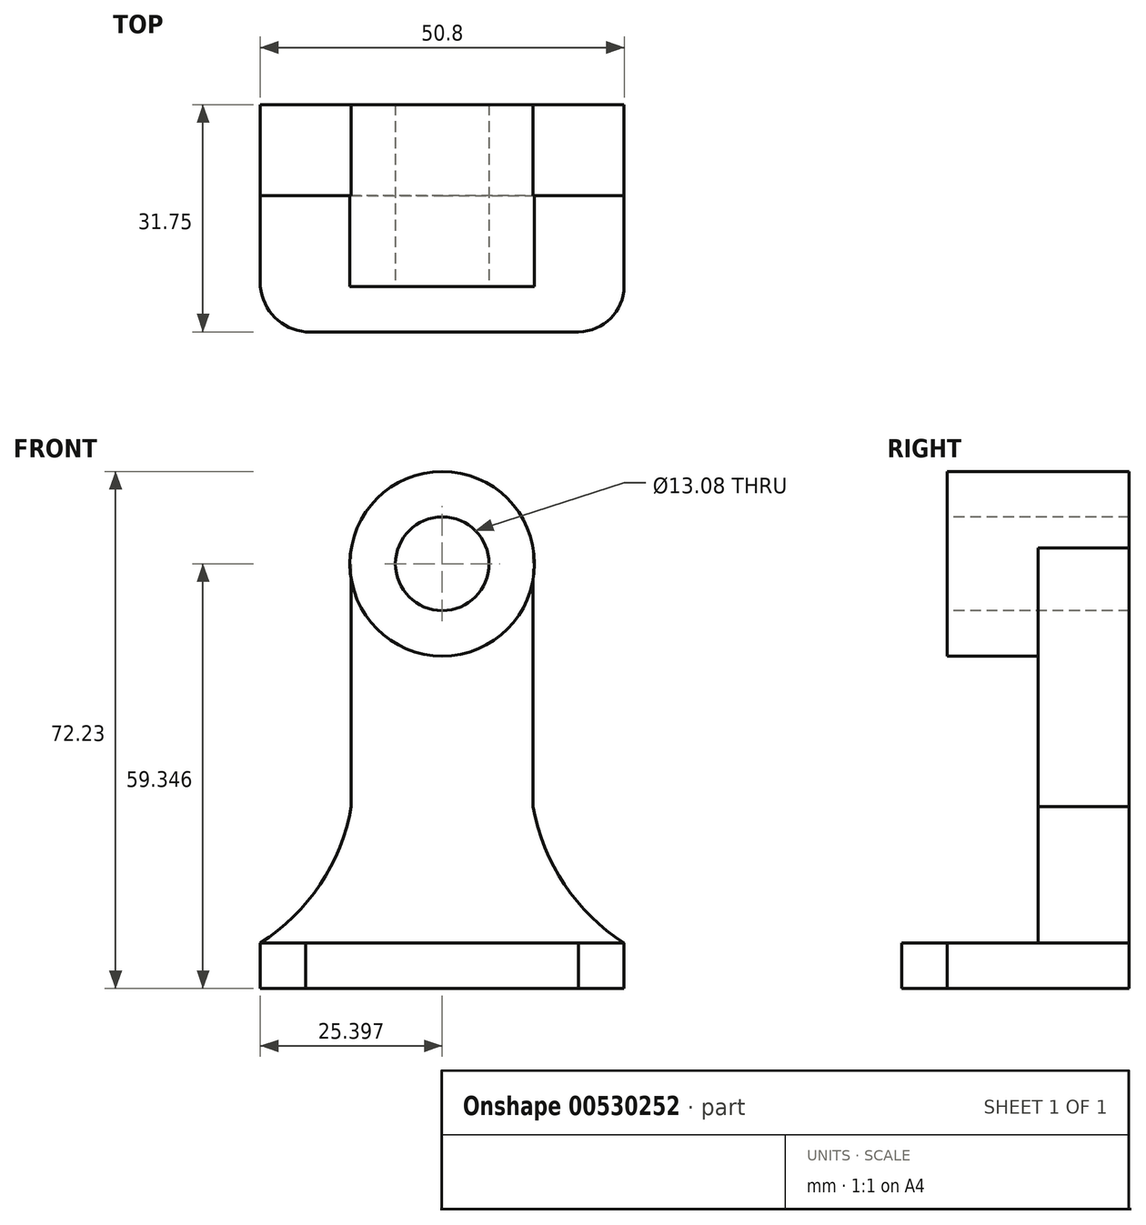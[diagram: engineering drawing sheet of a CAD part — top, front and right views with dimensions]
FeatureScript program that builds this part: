
annotation { "Feature Type Name" : "Feature", "Feature Type Description" : "" }
export const myFeature = defineFeature(function(context is Context, id is Id, definition is map)
    precondition{}
    {
        {
            var Q0;
            Q0=qCreatedBy(makeId("Front.planeOp"),FACE);
            var sketch = newSketch(context, id + "F0", { "sketchPlane" : qUnion([Q0])});
            skLineSegment(sketch, "E0", {"start": v(-66.08, 0) * mm, "end": v(-15.28, 0) * mm});
            skLineSegment(sketch, "E1", {"start": v(-15.28, 0) * mm, "end": v(-15.28, 6.35) * mm});
            skLineSegment(sketch, "E2", {"start": v(-15.28, 6.35) * mm, "end": v(-66.08, 6.35) * mm});
            skLineSegment(sketch, "E3", {"start": v(-66.08, 6.35) * mm, "end": v(-66.08, 0) * mm});
            skSolve(sketch);
        }
        {
            var Q0;
            Q0 = qSketchRegion(id + "F0", true);
            extrude(context, id + "F1", {"entities" : qUnion([Q0]), "depth" : 31.75 * mm, "offsetDistance" : 25.4 * mm});
        }
        {
            var Q0;
            Q0=makeQuery(id+"F1.opExtrude","CAP_FACE",FACE,{"disambiguationData":[OSD([sQuery(id+"F0.wireOp",EDGE,"E0"),sQuery(id+"F0.wireOp",EDGE,"E1"),sQuery(id+"F0.wireOp",EDGE,"E2"),sQuery(id+"F0.wireOp",EDGE,"E3")])],"isStart":true});
            var sketch = newSketch(context, id + "F2", { "sketchPlane" : qUnion([Q0])});
            skLineSegment(sketch, "E4", {"start": v(15.28, 6.35) * mm, "end": v(15.28, 76.2) * mm});
            skLineSegment(sketch, "E5", {"start": v(15.28, 76.2) * mm, "end": v(66.08, 76.2) * mm});
            skLineSegment(sketch, "E6", {"start": v(66.08, 76.2) * mm, "end": v(66.08, 6.35) * mm});
            skLineSegment(sketch, "E7", {"start": v(66.08, 6.35) * mm, "end": v(15.28, 6.35) * mm});
            skSolve(sketch);
        }
        {
            var Q0;
            Q0 = qSketchRegion(id + "F2", true);
            extrude(context, id + "F3", {"entities" : qUnion([Q0]), "operationType" : NewBodyOperationType.ADD, "oppositeDirection" : true, "depth" : 12.7 * mm, "offsetDistance" : 25.4 * mm});
        }
        {
            var Q0;
            Q0=makeQuery(id+"F3.opExtrude","CAP_FACE",FACE,{"disambiguationData":[OSD([sQuery(id+"F2.wireOp",EDGE,"E4"),sQuery(id+"F2.wireOp",EDGE,"E5"),sQuery(id+"F2.wireOp",EDGE,"E6"),sQuery(id+"F2.wireOp",EDGE,"E7")])],"isStart":false});
            var sketch = newSketch(context, id + "F4", { "sketchPlane" : qUnion([Q0])});
            skLineSegment(sketch, "E8", {"start": v(-53.38, 76.2) * mm, "end": v(-53.38, 6.35) * mm});
            skLineSegment(sketch, "E9", {"start": v(-53.38, 6.35) * mm, "end": v(-27.98, 6.35) * mm});
            skLineSegment(sketch, "E10", {"start": v(-27.98, 6.35) * mm, "end": v(-27.98, 76.2) * mm});
            skLineSegment(sketch, "E11", {"start": v(-27.98, 76.2) * mm, "end": v(-53.38, 76.2) * mm});
            skSolve(sketch);
        }
        {
            var Q0;
            {var subQ0=sQuery(id+"F4.wireOp",EDGE,"E8");Q0=makeQuery(id+"F4.imprint","IMPRINT",FACE,{"disambiguationData":[TD([[makeQuery(id+"F4.imprint","IMPRINT",EDGE,{"derivedFrom":subQ0}),-1.0]])]});}
            var Q1;
            {var subQ0=sQuery(id+"F4.wireOp",EDGE,"E10");Q1=makeQuery(id+"F4.imprint","IMPRINT",FACE,{"disambiguationData":[TD([[makeQuery(id+"F4.imprint","IMPRINT",EDGE,{"derivedFrom":subQ0}),-1.0]])]});}
            extrude(context, id + "F5", {"entities" : qUnion([Q0, Q1]), "operationType" : NewBodyOperationType.REMOVE, "oppositeDirection" : true, "depth" : 25.4 * mm, "offsetDistance" : 25.4 * mm});
        }
        {
            var Q0;
            Q0=makeQuery(id+"F3.boolean.opBoolean","MERGE",FACE,{"derivedFrom":[makeQuery(id+"F1.opExtrude","CAP_FACE",FACE,{"disambiguationData":[OSD([sQuery(id+"F0.wireOp",EDGE,"E0"),sQuery(id+"F0.wireOp",EDGE,"E1"),sQuery(id+"F0.wireOp",EDGE,"E2"),sQuery(id+"F0.wireOp",EDGE,"E3")])],"isStart":true}),makeQuery(id+"F3.opExtrude","CAP_FACE",FACE,{"disambiguationData":[OSD([sQuery(id+"F2.wireOp",EDGE,"E4"),sQuery(id+"F2.wireOp",EDGE,"E5"),sQuery(id+"F2.wireOp",EDGE,"E6"),sQuery(id+"F2.wireOp",EDGE,"E7")])],"isStart":true})]});
            var sketch = newSketch(context, id + "F6", { "sketchPlane" : qUnion([Q0])});
            skArc(sketch, "E12", {"start": v(15.28, 6.35) * mm, "mid": v(23.62, 14.55) * mm, "end": v(27.98, 25.4) * mm});
            skArc(sketch, "E13", {"start": v(53.38, 25.4) * mm, "mid": v(57.74, 14.55) * mm, "end": v(66.08, 6.35) * mm});
            skSolve(sketch);
        }
        {
            var Q0;
            Q0 = qSketchRegion(id + "F6", true);
            var Q1;
            {var subQ0=sQuery(id+"F6.wireOp",EDGE,"E12");Q1=makeQuery(id+"F6.imprint","IMPRINT",FACE,{"disambiguationData":[TD([[makeQuery(id+"F6.imprint","IMPRINT",EDGE,{"derivedFrom":subQ0}),-1.0]])]});}
            var Q2;
            {var subQ0=sQuery(id+"F6.wireOp",EDGE,"E13");Q2=makeQuery(id+"F6.imprint","IMPRINT",FACE,{"disambiguationData":[TD([[makeQuery(id+"F6.imprint","IMPRINT",EDGE,{"derivedFrom":subQ0}),-1.0]])]});}
            extrude(context, id + "F7", {"entities" : qUnion([Q0, Q1, Q2]), "operationType" : NewBodyOperationType.ADD, "oppositeDirection" : true, "depth" : 12.7 * mm, "offsetDistance" : 25.4 * mm});
        }
        {
            var Q0;
            {var subQ0=sQuery(id+"F2.wireOp",EDGE,"E7");var subQ1=sQuery(id+"F2.wireOp",EDGE,"E6");var subQ2=sQuery(id+"F2.wireOp",EDGE,"E5");var subQ3=sQuery(id+"F2.wireOp",EDGE,"E4");var subQ4=sQuery(id+"F0.wireOp",EDGE,"E3");var subQ5=sQuery(id+"F0.wireOp",EDGE,"E2");var subQ6=sQuery(id+"F0.wireOp",EDGE,"E1");var subQ7=sQuery(id+"F0.wireOp",EDGE,"E0");Q0=makeQuery(id+"F7.boolean.opBoolean","MERGE",FACE,{"derivedFrom":[makeQuery(id+"F3.opExtrude","CAP_FACE",FACE,{"disambiguationData":[OSD([subQ3,subQ2,subQ1,subQ0])],"isStart":false}),makeQuery(id+"F7.opExtrude","CAP_FACE",FACE,{"disambiguationData":[OSD([subQ7,subQ6,subQ5,subQ4,subQ3,subQ2,subQ1,subQ0,sQuery(id+"F4.wireOp",EDGE,"E10"),sQuery(id+"F6.wireOp",EDGE,"E12")])],"isStart":false}),makeQuery(id+"F7.opExtrude","CAP_FACE",FACE,{"disambiguationData":[OSD([subQ7,subQ6,subQ5,subQ4,subQ3,subQ2,subQ1,subQ0,sQuery(id+"F4.wireOp",EDGE,"E8"),sQuery(id+"F6.wireOp",EDGE,"E13")])],"isStart":false})]});}
            var sketch = newSketch(context, id + "F8", { "sketchPlane" : qUnion([Q0])});
            skArc(sketch, "E14", {"start": v(-27.98, 57.15) * mm, "mid": v(-40.68, 72.23) * mm, "end": v(-53.38, 57.15) * mm});
            skSolve(sketch);
        }
        {
            var Q0;
            {var subQ5=makeQuery(id+"F3.opExtrude","CAP_EDGE",EDGE,{"disambiguationData":[OSD([sQuery(id+"F2.wireOp",EDGE,"E5")])],"isStart":false});Q0=makeQuery(id+"F8.imprint","IMPRINT",FACE,{"disambiguationData":[TD([[makeQuery(id+"F8.imprint","IMPRINT",EDGE,{"derivedFrom":subQ5}),1.0]])]});}
            extrude(context, id + "F9", {"entities" : qUnion([Q0]), "operationType" : NewBodyOperationType.REMOVE, "endBound" : BoundingType.THROUGH_ALL, "oppositeDirection" : true, "depth" : 25.4 * mm, "offsetDistance" : 25.4 * mm});
        }
        {
            var Q0;
            {var subQ0=sQuery(id+"F2.wireOp",EDGE,"E7");var subQ1=sQuery(id+"F2.wireOp",EDGE,"E6");var subQ2=sQuery(id+"F2.wireOp",EDGE,"E5");var subQ3=sQuery(id+"F2.wireOp",EDGE,"E4");var subQ4=sQuery(id+"F0.wireOp",EDGE,"E3");var subQ5=sQuery(id+"F0.wireOp",EDGE,"E2");var subQ6=sQuery(id+"F0.wireOp",EDGE,"E1");var subQ7=sQuery(id+"F0.wireOp",EDGE,"E0");Q0=makeQuery(id+"F7.boolean.opBoolean","MERGE",FACE,{"derivedFrom":[makeQuery(id+"F3.opExtrude","CAP_FACE",FACE,{"disambiguationData":[OSD([subQ3,subQ2,subQ1,subQ0])],"isStart":false}),makeQuery(id+"F7.opExtrude","CAP_FACE",FACE,{"disambiguationData":[OSD([subQ7,subQ6,subQ5,subQ4,subQ3,subQ2,subQ1,subQ0,sQuery(id+"F4.wireOp",EDGE,"E10"),sQuery(id+"F6.wireOp",EDGE,"E12")])],"isStart":false}),makeQuery(id+"F7.opExtrude","CAP_FACE",FACE,{"disambiguationData":[OSD([subQ7,subQ6,subQ5,subQ4,subQ3,subQ2,subQ1,subQ0,sQuery(id+"F4.wireOp",EDGE,"E8"),sQuery(id+"F6.wireOp",EDGE,"E13")])],"isStart":false})]});}
            var sketch = newSketch(context, id + "F10", { "sketchPlane" : qUnion([Q0])});
            skCircle(sketch, "E15", {"center": v(-40.68, 59.35) * mm, "radius": 12.89 * mm});
            skSolve(sketch);
        }
        {
            var Q0;
            Q0 = qSketchRegion(id + "F10", true);
            extrude(context, id + "F11", {"entities" : qUnion([Q0]), "operationType" : NewBodyOperationType.ADD, "depth" : 12.7 * mm, "offsetDistance" : 25.4 * mm});
        }
        {
            var Q0;
            Q0=makeQuery(id+"F11.opExtrude","CAP_FACE",FACE,{"disambiguationData":[OSD([sQuery(id+"F10.wireOp",EDGE,"E15")])],"isStart":false});
            var sketch = newSketch(context, id + "F12", { "sketchPlane" : qUnion([Q0])});
            skCircle(sketch, "E16", {"center": v(-40.68, 59.35) * mm, "radius": 6.54 * mm});
            skSolve(sketch);
        }
        {
            var Q0;
            Q0 = qSketchRegion(id + "F12", true);
            extrude(context, id + "F13", {"entities" : qUnion([Q0]), "operationType" : NewBodyOperationType.REMOVE, "endBound" : BoundingType.THROUGH_ALL, "oppositeDirection" : true, "depth" : 25.4 * mm, "offsetDistance" : 25.4 * mm});
        }
        {
            var Q0;
            {var subQ0=sQuery(id+"F2.wireOp",EDGE,"E7");var subQ1=makeQuery(id+"F3.opExtrude","CAP_EDGE",EDGE,{"disambiguationData":[OSD([subQ0])],"isStart":false});Q0=makeQuery(id+"F5.boolean.opBoolean","MERGE",FACE,{"derivedFrom":[makeQuery(id+"F1.opExtrude","SWEPT_FACE",FACE,{"disambiguationData":[OSD([sQuery(id+"F0.wireOp",EDGE,"E2")])]}),makeQuery(id+"F5.opExtrude","SWEPT_FACE",FACE,{"disambiguationData":[OSD([subQ0]),TDD([makeQuery(id+"F4.imprint","IMPRINT",EDGE,{"disambiguationData":[TD([[makeQuery(id+"F4.imprint","INTERSECT",VERTEX,{"derivedFrom":[makeQuery(id+"F3.opExtrude","CAP_EDGE",EDGE,{"disambiguationData":[OSD([sQuery(id+"F2.wireOp",EDGE,"E4")])],"isStart":false}),subQ1]}),-1.0]])],"derivedFrom":subQ1})])]}),makeQuery(id+"F5.opExtrude","SWEPT_FACE",FACE,{"disambiguationData":[OSD([subQ0]),TDD([makeQuery(id+"F4.imprint","IMPRINT",EDGE,{"disambiguationData":[TD([[makeQuery(id+"F4.imprint","INTERSECT",VERTEX,{"derivedFrom":[makeQuery(id+"F3.opExtrude","CAP_EDGE",EDGE,{"disambiguationData":[OSD([sQuery(id+"F2.wireOp",EDGE,"E6")])],"isStart":false}),subQ1]}),1.0]])],"derivedFrom":subQ1})])]})]});}
            var sketch = newSketch(context, id + "F14", { "sketchPlane" : qUnion([Q0])});
            skArc(sketch, "E17", {"start": v(-21.63, -31.75) * mm, "mid": v(-17.17, -29.86) * mm, "end": v(-15.28, -25.4) * mm});
            skSolve(sketch);
        }
        {
            var Q0;
            Q0 = qSketchRegion(id + "F14", true);
            var Q1;
            {var subQ0=sQuery(id+"F14.wireOp",EDGE,"E17");Q1=makeQuery(id+"F14.imprint","IMPRINT",FACE,{"disambiguationData":[TD([[makeQuery(id+"F14.imprint","IMPRINT",EDGE,{"derivedFrom":subQ0}),-1.0]])]});}
            extrude(context, id + "F15", {"entities" : qUnion([Q0, Q1]), "operationType" : NewBodyOperationType.REMOVE, "oppositeDirection" : true, "depth" : 25.4 * mm, "offsetDistance" : 25.4 * mm});
        }
        {
            var Q0;
            {var subQ0=sQuery(id+"F2.wireOp",EDGE,"E7");var subQ1=makeQuery(id+"F3.opExtrude","CAP_EDGE",EDGE,{"disambiguationData":[OSD([subQ0])],"isStart":false});Q0=makeQuery(id+"F5.boolean.opBoolean","MERGE",FACE,{"derivedFrom":[makeQuery(id+"F1.opExtrude","SWEPT_FACE",FACE,{"disambiguationData":[OSD([sQuery(id+"F0.wireOp",EDGE,"E2")])]}),makeQuery(id+"F5.opExtrude","SWEPT_FACE",FACE,{"disambiguationData":[OSD([subQ0]),TDD([makeQuery(id+"F4.imprint","IMPRINT",EDGE,{"disambiguationData":[TD([[makeQuery(id+"F4.imprint","INTERSECT",VERTEX,{"derivedFrom":[makeQuery(id+"F3.opExtrude","CAP_EDGE",EDGE,{"disambiguationData":[OSD([sQuery(id+"F2.wireOp",EDGE,"E4")])],"isStart":false}),subQ1]}),-1.0]])],"derivedFrom":subQ1})])]}),makeQuery(id+"F5.opExtrude","SWEPT_FACE",FACE,{"disambiguationData":[OSD([subQ0]),TDD([makeQuery(id+"F4.imprint","IMPRINT",EDGE,{"disambiguationData":[TD([[makeQuery(id+"F4.imprint","INTERSECT",VERTEX,{"derivedFrom":[makeQuery(id+"F3.opExtrude","CAP_EDGE",EDGE,{"disambiguationData":[OSD([sQuery(id+"F2.wireOp",EDGE,"E6")])],"isStart":false}),subQ1]}),1.0]])],"derivedFrom":subQ1})])]})]});}
            var sketch = newSketch(context, id + "F16", { "sketchPlane" : qUnion([Q0])});
            skArc(sketch, "E18", {"start": v(-66.08, -25.4) * mm, "mid": v(-64.06, -29.73) * mm, "end": v(-59.73, -31.75) * mm});
            skSolve(sketch);
        }
        {
            var Q0;
            Q0 = qSketchRegion(id + "F16", true);
            var Q1;
            {var subQ0=sQuery(id+"F16.wireOp",EDGE,"E18");Q1=makeQuery(id+"F16.imprint","IMPRINT",FACE,{"disambiguationData":[TD([[makeQuery(id+"F16.imprint","IMPRINT",EDGE,{"derivedFrom":subQ0}),-1.0]])]});}
            extrude(context, id + "F17", {"entities" : qUnion([Q0, Q1]), "operationType" : NewBodyOperationType.REMOVE, "oppositeDirection" : true, "depth" : 25.4 * mm, "offsetDistance" : 25.4 * mm});
        }
    });
